# Revit family: Theater-Seat
name_source: partatom
category: Generic Models
units: mm (PartAtom-declared; Revit-internal decimal feet)

## family parameters
Always vertical = Yes
Can host rebar = No
Classification Number = 23.40.50.11.11
Cut with Voids When Loaded = No
Maintain Annotation Orientation = No
Part Type = Normal
Room Calculation Point = No
Round Connector Dimension = Use Diameter
Shared = No
Work Plane-Based = No

## types (3) — shared parameters
Assembly Code = E2010500
Construction Details = http://www.arcat.com
Default Elevation = 0' - 0"
Description = Theater Seat
Expected Lifespan (Years) = 10
Green Building-LEED = http://www.arcat.com
Keynote = 12610
Maintenance Schedule (Months) = 6
Manufacturer = Generic
Manufacturer Fax = (203) 939-2444
Manufacturer Website = http://www.arcat.com
Model = Generic
Product Data = http://www.arcat.com
Product Properties = http://www.arcat.com
Seat Closure = Self Closing
Seat Frame Material = ARCAT - Plastic - HDLP - Black
Specification = http://www.arcat.com
Stand Material = ARCAT - Metal - Steel 14ga - Painted - Black
Standards = California TB-117, ASTM F-851 (impact and static)
Static Test Load = 800 Lbs at Seat Edge
Warranty Duration (Years) = 1

## per-type parameters (varying)
| type | Padding |
| Burgundy-Black |  |
| Blue-Black |  |
| Green-Black | Molded resilient polyurethane foam |

## geometry (parser evidence)
native form markers: Sweep x5
no freeform markers — native parametric forms only
